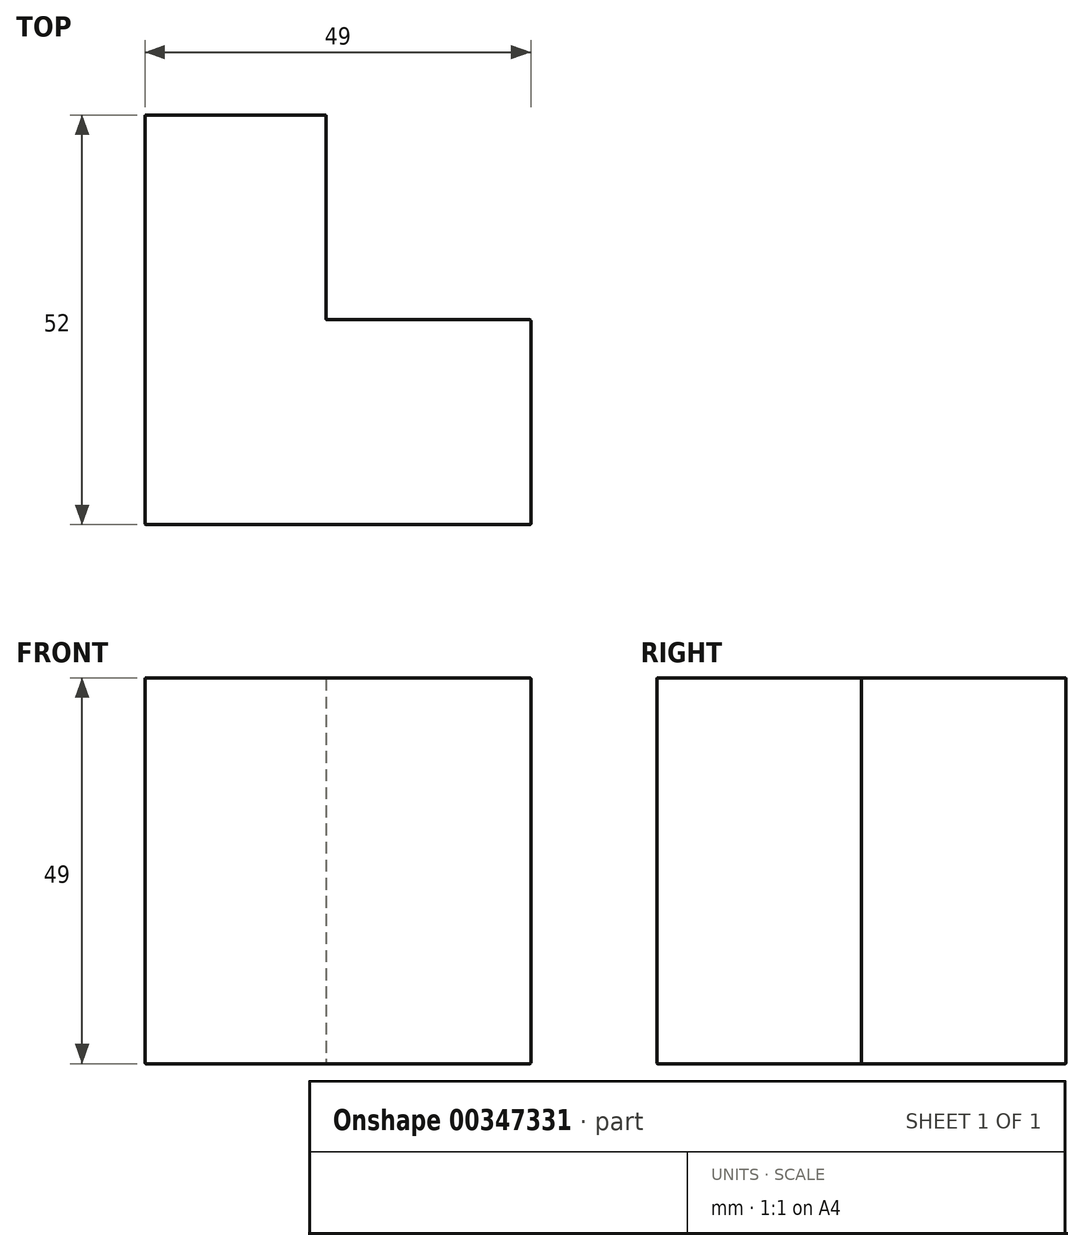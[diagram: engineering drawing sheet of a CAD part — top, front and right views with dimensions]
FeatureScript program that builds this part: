
annotation { "Feature Type Name" : "Feature", "Feature Type Description" : "" }
export const myFeature = defineFeature(function(context is Context, id is Id, definition is map)
    precondition{}
    {
        {
            var Q0;
            Q0=qCreatedBy(makeId("Top.planeOp"),FACE);
            var sketch = newSketch(context, id + "F0", { "sketchPlane" : qUnion([Q0])});
            skLineSegment(sketch, "E0.bottom", {"start": v(24.5, -13) * mm, "end": v(-24.5, -13) * mm});
            skLineSegment(sketch, "E0.top", {"start": v(24.5, 13) * mm, "end": v(-24.5, 13) * mm});
            skLineSegment(sketch, "E0.left", {"start": v(24.5, -13) * mm, "end": v(24.5, 13) * mm});
            skLineSegment(sketch, "E0.right", {"start": v(-24.5, -13) * mm, "end": v(-24.5, 13) * mm});
            skPoint(sketch, "E0.middle", {"position": v(0, 0) * mm});
            skLineSegment(sketch, "E1.bottom", {"start": v(-24.5, 13) * mm, "end": v(-1.5, 13) * mm});
            skLineSegment(sketch, "E1.top", {"start": v(-24.5, 39) * mm, "end": v(-1.5, 39) * mm});
            skLineSegment(sketch, "E1.left", {"start": v(-24.5, 13) * mm, "end": v(-24.5, 39) * mm});
            skLineSegment(sketch, "E1.right", {"start": v(-1.5, 13) * mm, "end": v(-1.5, 39) * mm});
            skSolve(sketch);
        }
        {
            var Q0;
            Q0 = qSketchRegion(id + "F0", true);
            extrude(context, id + "F1", {"entities" : qUnion([Q0]), "depth" : 49 * mm});
        }
        {
            var Q0;
            Q0=makeQuery(id+"F1.opExtrude","CAP_FACE",FACE,{"disambiguationData":[OSD([sQuery(id+"F0.wireOp",EDGE,"E0.bottom"),sQuery(id+"F0.wireOp",EDGE,"E0.top"),sQuery(id+"F0.wireOp",EDGE,"E0.left"),sQuery(id+"F0.wireOp",EDGE,"E0.right"),sQuery(id+"F0.wireOp",EDGE,"E1.top"),sQuery(id+"F0.wireOp",EDGE,"E1.left"),sQuery(id+"F0.wireOp",EDGE,"E1.right")])],"isStart":false});
            var Q1;
            Q1=makeQuery(id+"F1.opExtrude","SWEPT_FACE",FACE,{"disambiguationData":[OSD([sQuery(id+"F0.wireOp",EDGE,"E0.left")])]});
            var Q2;
            Q2=makeQuery(id+"F1.opExtrude","SWEPT_FACE",FACE,{"disambiguationData":[OSD([sQuery(id+"F0.wireOp",EDGE,"E0.top")])]});
            var Q3;
            Q3=makeQuery(id+"F1.opExtrude","SWEPT_FACE",FACE,{"disambiguationData":[OSD([sQuery(id+"F0.wireOp",EDGE,"E1.right")])]});
            var Q4;
            Q4=makeQuery(id+"F1.opExtrude","SWEPT_FACE",FACE,{"disambiguationData":[OSD([sQuery(id+"F0.wireOp",EDGE,"E1.top")])]});
            var Q5;
            Q5=makeQuery(id+"F1.opExtrude","SWEPT_FACE",FACE,{"disambiguationData":[OSD([sQuery(id+"F0.wireOp",EDGE,"E0.right"),sQuery(id+"F0.wireOp",EDGE,"E1.left")])]});
            var Q6;
            Q6=makeQuery(id+"F1.opExtrude","CAP_EDGE",EDGE,{"disambiguationData":[OSD([sQuery(id+"F0.wireOp",EDGE,"E0.bottom")])],"isStart":true});
            fillet(context, id + "F2", {"entities" : qUnion([Q0, Q1, Q2, Q3, Q4, Q5, Q6]), "radius" : 0.1 * mm, "tangentPropagation" : true, "allowEdgeOverflow" : false});
        }
    });
